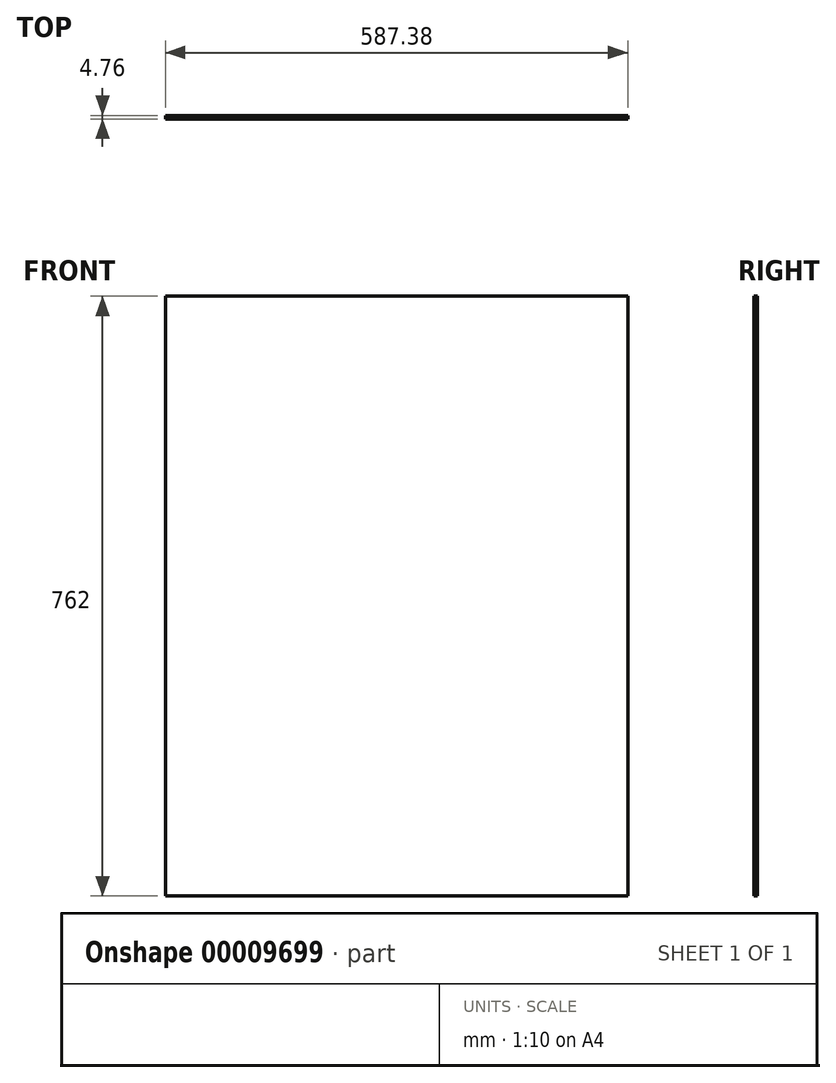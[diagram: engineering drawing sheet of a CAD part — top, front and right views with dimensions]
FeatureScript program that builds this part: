
annotation { "Feature Type Name" : "Feature", "Feature Type Description" : "" }
export const myFeature = defineFeature(function(context is Context, id is Id, definition is map)
    precondition{}
    {
        {
            var Q0;
            Q0=qCreatedBy(makeId("Front.planeOp"),FACE);
            var sketch = newSketch(context, id + "F0", { "sketchPlane" : qUnion([Q0])});
            skLineSegment(sketch, "E0.rect.bottom", {"start": v(293.69, 381) * mm, "end": v(-293.69, 381) * mm});
            skLineSegment(sketch, "E0.rect.top", {"start": v(293.69, -381) * mm, "end": v(-293.69, -381) * mm});
            skLineSegment(sketch, "E0.rect.left", {"start": v(293.69, 381) * mm, "end": v(293.69, -381) * mm});
            skLineSegment(sketch, "E0.rect.right", {"start": v(-293.69, 381) * mm, "end": v(-293.69, -381) * mm});
            skPoint(sketch, "E0.rect.middle", {"position": v(0, 0) * mm});
            skSolve(sketch);
        }
        {
            var Q0;
            Q0=makeQuery(id+"F0.imprint","IMPRINT",FACE,{"disambiguationData":[TD([[makeQuery(id+"F0.imprint","IMPRINT",EDGE,{"derivedFrom":sQuery(id+"F0.wireOp",EDGE,"E0.rect.bottom")}),1.0]])]});
            extrude(context, id + "F1", {"entities" : qUnion([Q0]), "depth" : 4.76 * mm});
        }
    });
